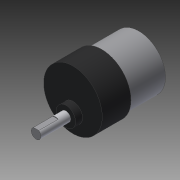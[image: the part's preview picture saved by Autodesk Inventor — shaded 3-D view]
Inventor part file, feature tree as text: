
AUTODESK INVENTOR PART (.ipt)
format: ipt  version: 2014 SP1 (Build 180222100, 222)  size: 134,656 bytes
history: native  units: in
note: dims shown in document units (in); Inventor stores cm internally (conversion verified against a paired STEP export)
features: sketch x7, other x3
ambient origin geometry x8: Origin, YZ Plane, XZ Plane, XY Plane, X Axis, Y Axis, Z Axis, Center Point
bodies: Solid1 (feature_tree)
feature tree (10):
  other  "Drive Motor.ipt"
  other  "Solid1::Drive Motor.ipt"
  other  "TaggingFeature1"
  sketch  "Sketch1"  dims[d0=0.3937in]
  sketch  "Sketch2"  dims[d1=0.7in d2=0.0in d3=0.449in d4=0.47in d5=0.17in d6=0.0in d7=0.2362in d8=0.725in d9=0.0in d11=0.4724in d12=0.0in d13=1.3in d14=0.9in d15=0.0in d16=0.35in d17=0.125in d18=0.0in d21=0.1181in d22=0.1181in d23=2.114in d24=2.114in d25=0.1181in d26=0.1181in d27=0.5in d28=0.0in]
  sketch  "Sketch3"
  sketch  "Sketch4"
  sketch  "Sketch5"
  sketch  "Sketch6"
  sketch  "Sketch7"
